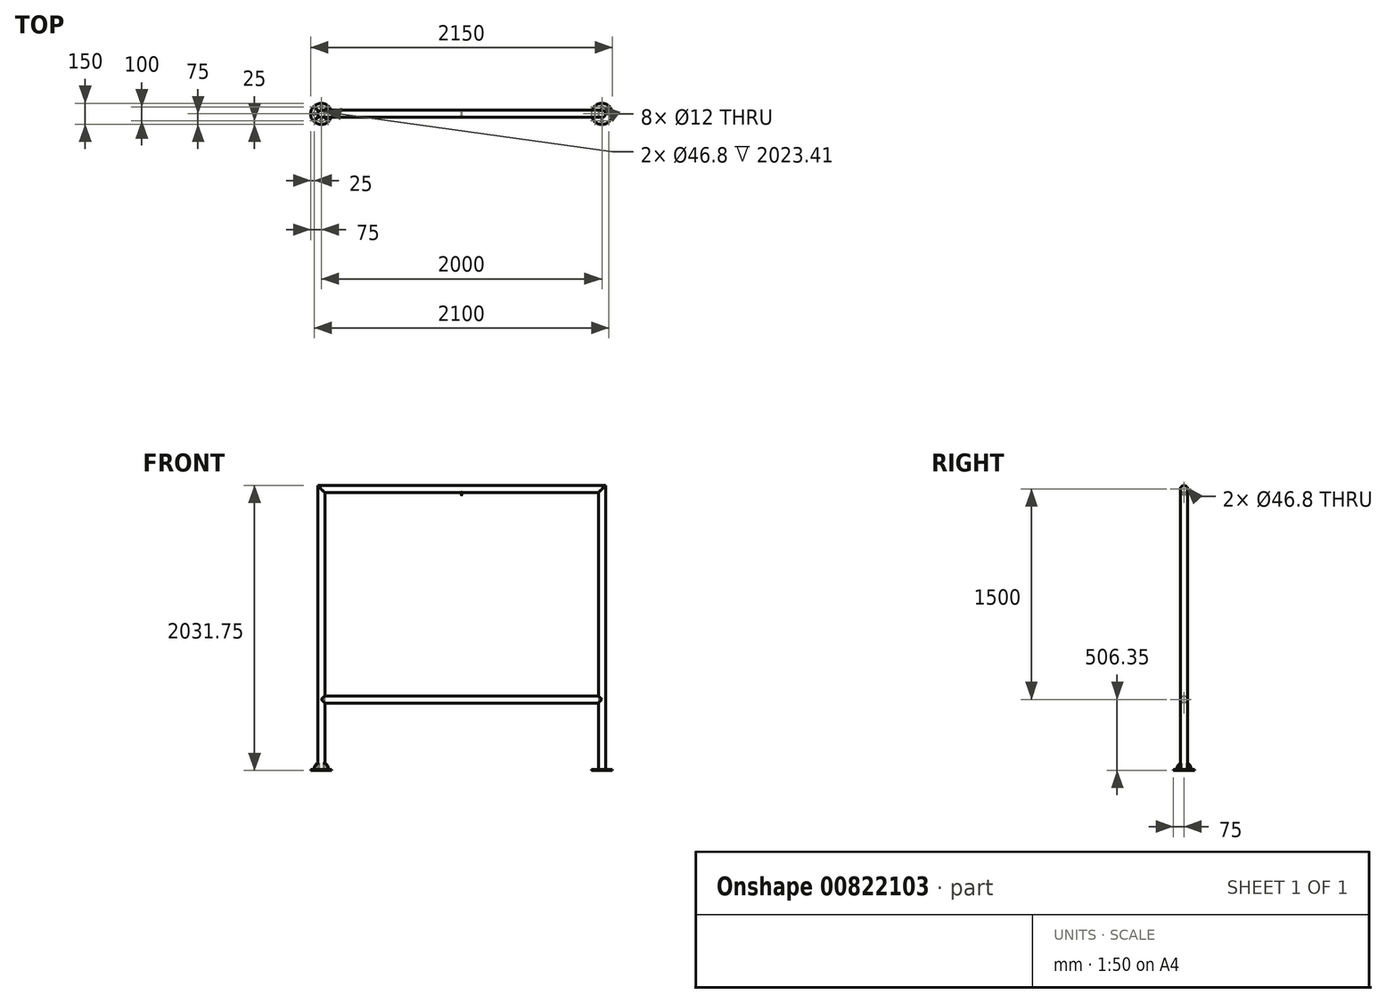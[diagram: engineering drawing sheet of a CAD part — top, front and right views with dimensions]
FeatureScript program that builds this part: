
annotation { "Feature Type Name" : "Feature", "Feature Type Description" : "" }
export const myFeature = defineFeature(function(context is Context, id is Id, definition is map)
    precondition{}
    {
        {
            var Q0;
            Q0=qCreatedBy(makeId("Front.planeOp"),FACE);
            var sketch = newSketch(context, id + "F0", { "sketchPlane" : qUnion([Q0])});
            skLineSegment(sketch, "E0", {"start": v(0, 0) * mm, "end": v(0, 2000) * mm});
            skLineSegment(sketch, "E1", {"start": v(0, 2000) * mm, "end": v(2000, 2000) * mm});
            skLineSegment(sketch, "E2", {"start": v(2000, 2000) * mm, "end": v(2000, 0) * mm});
            skPoint(sketch, "E3.visualSharp", {"position": v(0, 2000) * mm});
            skPoint(sketch, "E4.visualSharp", {"position": v(2000, 2000) * mm});
            skSolve(sketch);
        }
        {
            var Q0;
            Q0=qCreatedBy(makeId("Top.planeOp"),FACE);
            var sketch = newSketch(context, id + "F1", { "sketchPlane" : qUnion([Q0])});
            skCircle(sketch, "E5", {"center": v(0, 0) * mm, "radius": 25.4 * mm});
            skCircle(sketch, "E6", {"center": v(0, 0) * mm, "radius": 23.4 * mm});
            skSolve(sketch);
        }
        {
            var Q0;
            Q0=makeQuery(id+"F1.imprint","IMPRINT",FACE,{"disambiguationData":[TD([[makeQuery(id+"F1.imprint","IMPRINT",EDGE,{"derivedFrom":sQuery(id+"F1.wireOp",EDGE,"E5")}),1.0]])]});
            var Q1;
            Q1=sQuery(id+"F0.wireOp",EDGE,"E0");
            var Q2;
            Q2=sQuery(id+"F0.wireOp",EDGE,"E3.filletArc");
            var Q3;
            Q3=sQuery(id+"F0.wireOp",EDGE,"E1");
            var Q4;
            Q4=sQuery(id+"F0.wireOp",EDGE,"E4.filletArc");
            var Q5;
            Q5=sQuery(id+"F0.wireOp",EDGE,"E2");
            sweep(context, id + "F2", {"profiles" : qUnion([Q0]), "path" : qUnion([Q1, Q2, Q3, Q4, Q5])});
        }
        {
            var Q0;
            Q0=qCreatedBy(makeId("Right.planeOp"),FACE);
            cPlane(context, id + "F3", {"entities" : qUnion([Q0]), "cplaneType" : CPlaneType.OFFSET, "offset" : 1000 * mm, "width" : 150 * mm, "height" : 150 * mm});
        }
        {
            var Q0;
            Q0=qCreatedBy(id+"F3.planeOp",FACE);
            var sketch = newSketch(context, id + "F4", { "sketchPlane" : qUnion([Q0])});
            skCircle(sketch, "E7", {"center": v(0, 500) * mm, "radius": 25.4 * mm});
            skCircle(sketch, "E8", {"center": v(0, 500) * mm, "radius": 23.4 * mm});
            skSolve(sketch);
        }
        {
            var Q0;
            Q0 = qSketchRegion(id + "F4", true);
            var Q1;
            Q1=makeQuery(id+"F2.opSweep","SWEPT_FACE",FACE,{"disambiguationData":[OSD([sQuery(id+"F0.wireOp",EDGE,"E2"),sQuery(id+"F1.wireOp",EDGE,"E5")])]});
            var Q2;
            Q2=makeQuery(id+"F2.opSweep","SWEPT_FACE",FACE,{"disambiguationData":[OSD([sQuery(id+"F0.wireOp",EDGE,"E0"),sQuery(id+"F1.wireOp",EDGE,"E5")])]});
            extrude(context, id + "F5", {"entities" : qUnion([Q0]), "operationType" : NewBodyOperationType.ADD, "endBound" : BoundingType.UP_TO_SURFACE, "depth" : 25 * mm, "endBoundEntityFace" : qUnion([Q1]), "offsetDistance" : 25 * mm, "hasSecondDirection" : true, "secondDirectionBound" : SecondDirectionBoundingType.UP_TO_SURFACE, "secondDirectionOppositeDirection" : true, "secondDirectionDepth" : 25 * mm, "secondDirectionBoundEntityFace" : qUnion([Q2])});
        }
        {
            var Q0;
            Q0=makeQuery(id+"F2.opSweep","CAP_FACE",FACE,{"disambiguationData":[OSD([sQuery(id+"F0.wireOp",VERTEX,"E0.start"),sQuery(id+"F1.wireOp",EDGE,"E5"),sQuery(id+"F1.wireOp",EDGE,"E6")])],"isStart":true});
            var sketch = newSketch(context, id + "F6", { "sketchPlane" : qUnion([Q0])});
            skCircle(sketch, "E9", {"center": v(0, 0) * mm, "radius": 75 * mm});
            skCircle(sketch, "E10", {"center": v(2000, 0) * mm, "radius": 75 * mm});
            skSolve(sketch);
        }
        {
            var Q0;
            Q0 = qSketchRegion(id + "F6", true);
            extrude(context, id + "F7", {"entities" : qUnion([Q0]), "operationType" : NewBodyOperationType.ADD, "depth" : 6.35 * mm, "offsetDistance" : 25 * mm});
        }
        {
            var Q0;
            Q0=makeQuery(id+"F7.opExtrude","CAP_FACE",FACE,{"disambiguationData":[OSD([sQuery(id+"F6.wireOp",EDGE,"E9")])],"isStart":false});
            var sketch = newSketch(context, id + "F8", { "sketchPlane" : qUnion([Q0])});
            skCircle(sketch, "E11", {"center": v(0, 0) * mm, "radius": 50 * mm, "construction": true});
            skCircle(sketch, "E12", {"center": v(0, 50) * mm, "radius": 6 * mm});
            skCircle(sketch, "E13", {"center": v(-50, 0) * mm, "radius": 6 * mm});
            skCircle(sketch, "E14", {"center": v(0, -50) * mm, "radius": 6 * mm});
            skCircle(sketch, "E15", {"center": v(50, 0) * mm, "radius": 6 * mm});
            skCircle(sketch, "E16", {"center": v(2000, 0) * mm, "radius": 50 * mm, "construction": true});
            skCircle(sketch, "E17", {"center": v(2000, 50) * mm, "radius": 6 * mm});
            skCircle(sketch, "E18", {"center": v(2000, -50) * mm, "radius": 6 * mm});
            skCircle(sketch, "E19", {"center": v(2050, 0) * mm, "radius": 6 * mm});
            skCircle(sketch, "E20", {"center": v(1950, 0) * mm, "radius": 6 * mm});
            skSolve(sketch);
        }
        {
            var Q0;
            Q0 = qSketchRegion(id + "F8", true);
            extrude(context, id + "F9", {"entities" : qUnion([Q0]), "operationType" : NewBodyOperationType.REMOVE, "oppositeDirection" : true, "depth" : 25 * mm, "offsetDistance" : 25 * mm});
        }
        {
            var Q0;
            Q0=sQuery(id+"F0.wireOp",EDGE,"E0");
            var Q1;
            Q1=qCreatedBy(makeId("Front.planeOp"),FACE);
            cPlane(context, id + "F10", {"entities" : qUnion([Q0, Q1]), "cplaneType" : CPlaneType.LINE_ANGLE, "offset" : 25 * mm, "angle" : 45 * degree, "width" : 150 * mm, "height" : 150 * mm});
        }
        {
            var Q0;
            Q0=qCreatedBy(id+"F10.planeOp",FACE);
            var sketch = newSketch(context, id + "F11", { "sketchPlane" : qUnion([Q0])});
            skArc(sketch, "E21", {"start": v(69.4, 0) * mm, "mid": v(56.22, 31.82) * mm, "end": v(24.4, 45) * mm});
            skLineSegment(sketch, "E22", {"start": v(24.4, 45) * mm, "end": v(24.4, 0) * mm});
            skLineSegment(sketch, "E23", {"start": v(24.4, 0) * mm, "end": v(69.4, 0) * mm});
            skSolve(sketch);
        }
        {
            var Q0;
            Q0 = qSketchRegion(id + "F11", true);
            extrude(context, id + "F12", {"entities" : qUnion([Q0]), "endBound" : BoundingType.SYMMETRIC, "depth" : 6 * mm, "offsetDistance" : 25 * mm});
        }
        {
            var Q0;
            Q0=qCreatedBy(makeId("Front.planeOp"),FACE);
            var sketch = newSketch(context, id + "F13", { "sketchPlane" : qUnion([Q0])});
            skLineSegment(sketch, "E24", {"start": v(0, 0) * mm, "end": v(0, 2000) * mm, "construction": true});
            skLineSegment(sketch, "E25.0", {"start": v(25.4, 1974.6) * mm, "end": v(-25.4, 2025.4) * mm, "construction": true});
            skSolve(sketch);
        }
        {
            var Q0;
            Q0=makeQuery(id+"F12.opExtrude","SWEPT_BODY",BODY,{"disambiguationData":[OSD([sQuery(id+"F11.wireOp",EDGE,"E21"),sQuery(id+"F11.wireOp",EDGE,"E22"),sQuery(id+"F11.wireOp",EDGE,"E23")])]});
            var Q1;
            Q1=sQuery(id+"F13.wireOp",EDGE,"E24");
            circularPattern(context, id + "F14", {"entities" : qUnion([Q0]), "axis" : qUnion([Q1]), "angle" : 360 * degree, "instanceCount" : 4, "equalSpace" : true});
        }
        {
            var Q0;
            Q0=qCreatedBy(id+"F3.planeOp",FACE);
            var sketch = newSketch(context, id + "F15", { "sketchPlane" : qUnion([Q0])});
            skLineSegment(sketch, "E26", {"start": v(8, 1978.01) * mm, "end": v(8, 1966.01) * mm});
            skLineSegment(sketch, "E27", {"start": v(-8, 1978.01) * mm, "end": v(-8, 1966.01) * mm});
            skArc(sketch, "E28", {"start": v(-8, 1966.01) * mm, "mid": v(0, 1958.01) * mm, "end": v(8, 1966.01) * mm});
            skCircle(sketch, "E29.0", {"center": v(0, 2000) * mm, "radius": 23.4 * mm, "construction": true});
            skLineSegment(sketch, "E30", {"start": v(0, 2000) * mm, "end": v(0, 1966.01) * mm, "construction": true});
            skSolve(sketch);
        }
        {
            var Q0;
            Q0=qCreatedBy(makeId("Top.planeOp"),FACE);
            var Q1;
            Q1=sQuery(id+"F15.wireOp",VERTEX,"E26.start");
            cPlane(context, id + "F16", {"entities" : qUnion([Q0, Q1]), "cplaneType" : CPlaneType.PLANE_POINT, "offset" : 25 * mm, "width" : 150 * mm, "height" : 150 * mm});
        }
        {
            var Q0;
            Q0=qCreatedBy(id+"F16.planeOp",FACE);
            var sketch = newSketch(context, id + "F17", { "sketchPlane" : qUnion([Q0])});
            skCircle(sketch, "E31", {"center": v(1000, -8) * mm, "radius": 2.5 * mm});
            skSolve(sketch);
        }
        {
            var Q0;
            Q0 = qSketchRegion(id + "F17", true);
            var Q1;
            Q1 = qConstructionFilter(qBodyType(qCreatedBy(id + "F15" ,EDGE), BodyType.WIRE), ConstructionObject.NO);
            sweep(context, id + "F18", {"operationType" : NewBodyOperationType.ADD, "profiles" : qUnion([Q0]), "path" : qUnion([Q1])});
        }
    });
